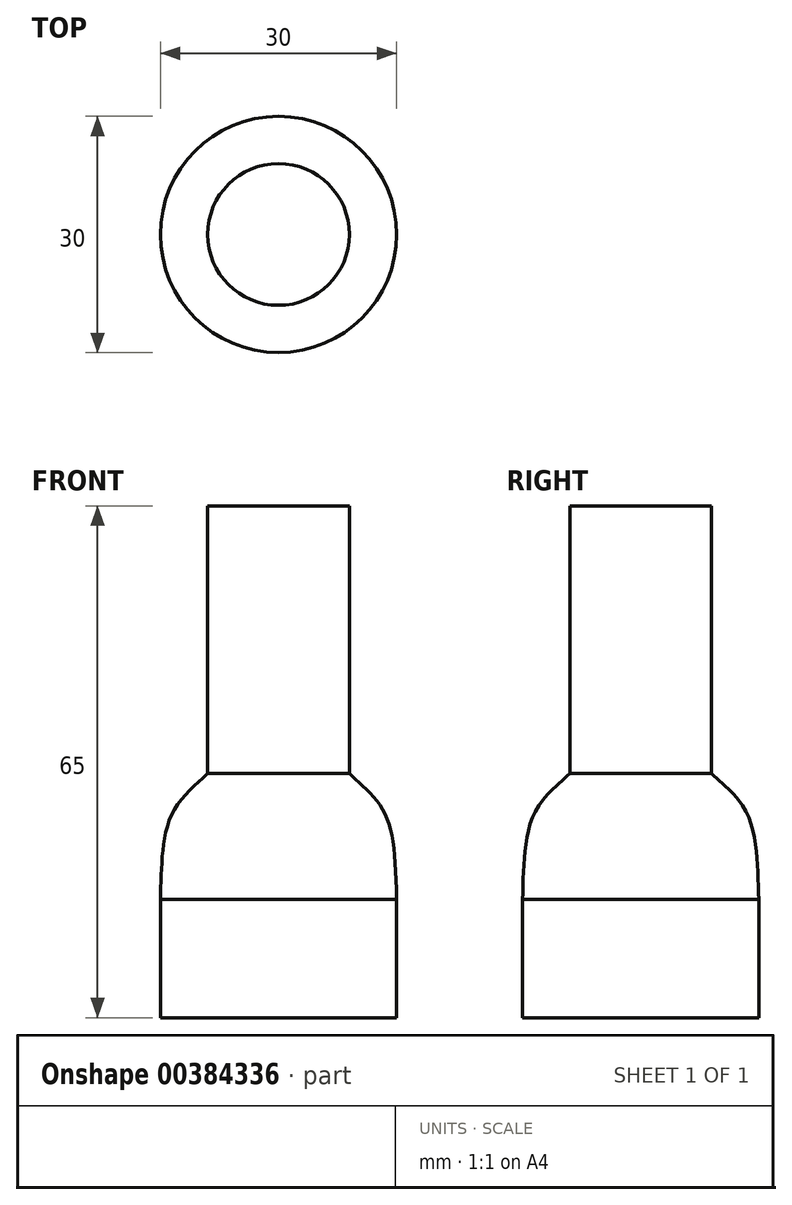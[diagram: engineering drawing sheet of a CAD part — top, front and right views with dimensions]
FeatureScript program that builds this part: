
annotation { "Feature Type Name" : "Feature", "Feature Type Description" : "" }
export const myFeature = defineFeature(function(context is Context, id is Id, definition is map)
    precondition{}
    {
        {
            var Q0;
            Q0=qCreatedBy(makeId("Front.planeOp"),FACE);
            var sketch = newSketch(context, id + "F0", { "sketchPlane" : qUnion([Q0])});
            skLineSegment(sketch, "E0", {"start": v(0, 65) * mm, "end": v(-9, 65) * mm});
            skLineSegment(sketch, "E1", {"start": v(-9, 65) * mm, "end": v(-9, 31) * mm});
            skLineSegment(sketch, "E2", {"start": v(0, 0) * mm, "end": v(0, 0) * mm});
            skLineSegment(sketch, "E3", {"start": v(-15, 15) * mm, "end": v(-15, 0) * mm});
            skLineSegment(sketch, "E4", {"start": v(-15, 0) * mm, "end": v(0, 0) * mm});
            skLineSegment(sketch, "E5", {"start": v(0, 65) * mm, "end": v(0, 0) * mm});
            skFitSpline(sketch, "E6", {"points": [v(-9, 31) * mm, v(-13.06, 26.74) * mm, v(-15, 15) * mm], "startDerivative": vector(-8.41, -7.8) * mm, "endDerivative": vector(-0.72, -30.44) * mm});
            skSolve(sketch);
        }
        {
            var Q0;
            Q0=makeQuery(id+"F0.imprint","IMPRINT",FACE,{"disambiguationData":[TD([[makeQuery(id+"F0.imprint","IMPRINT",EDGE,{"derivedFrom":sQuery(id+"F0.wireOp",EDGE,"E0")}),1.0]])]});
            var Q1;
            Q1=sQuery(id+"F0.wireOp",EDGE,"E5");
            revolve(context, id + "F1", {"entities" : qUnion([Q0]), "axis" : qUnion([Q1]), "revolveType" : RevolveType.FULL});
        }
    });
